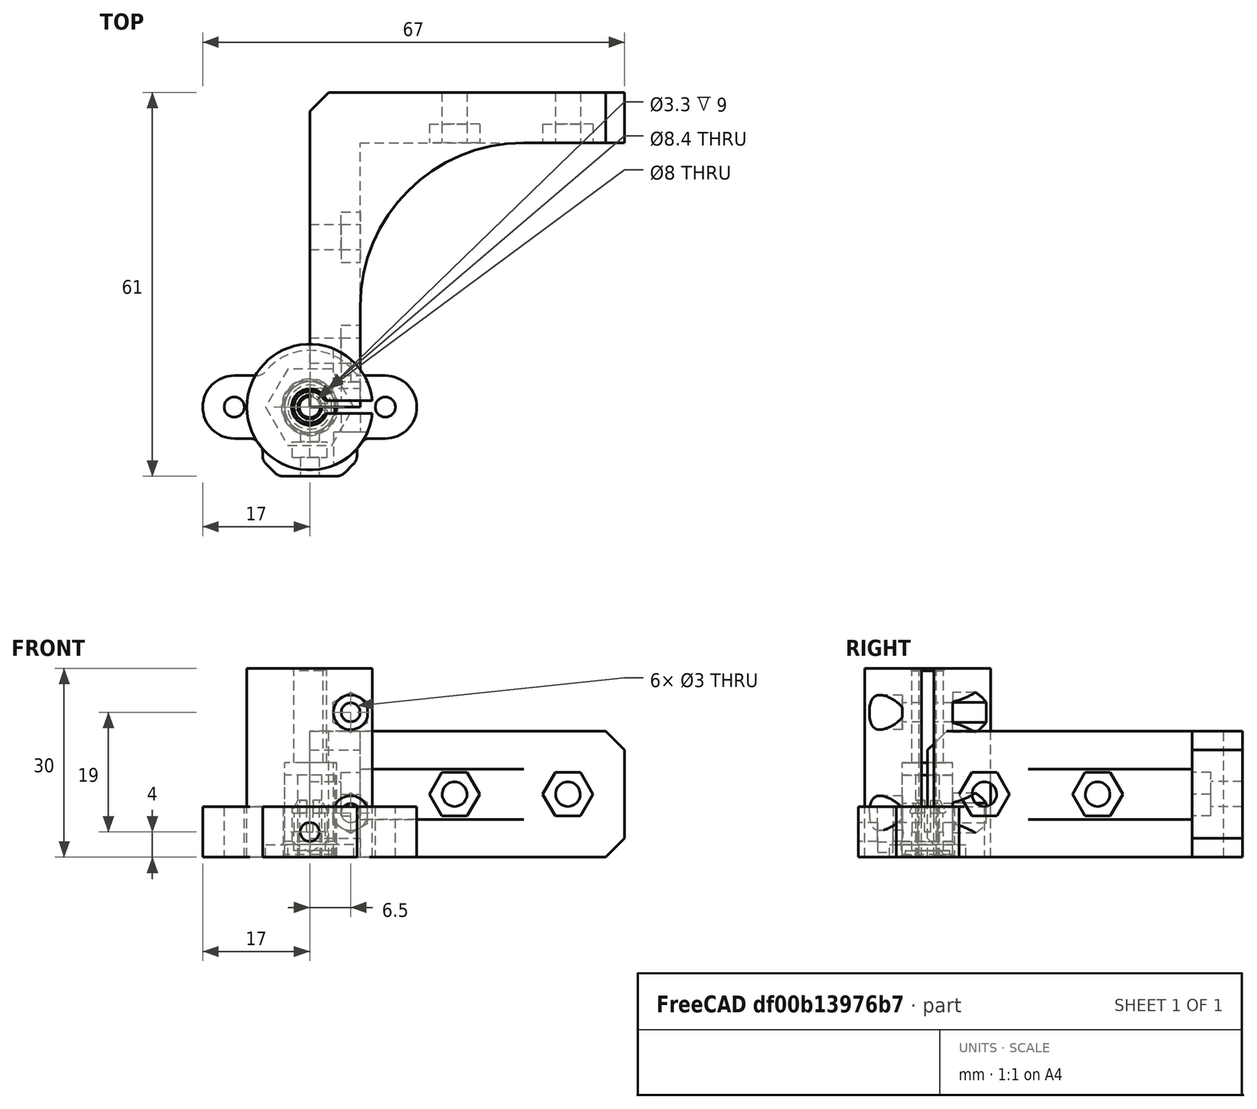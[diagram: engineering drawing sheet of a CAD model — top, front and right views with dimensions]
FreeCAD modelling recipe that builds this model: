
FCSTD DOCUMENT  (FreeCAD 0.16R6712 (Git))
Label: parts
License: All rights reserved
LicenseURL: http://en.wikipedia.org/wiki/All_rights_reserved
objects: Part::Cylinder×14, Part::MultiFuse×13, Part::Cut×9, Part::Chamfer×4, Part::Box×4, Sketcher::SketchObject×3, PartDesign::Pad×3, Part::Prism×3, Part::Fillet×3, Mesh::Feature×1, Part::Cone×1
note: 60 computed .brp shape members not serialized (recipe doc carries the construction recipe); baked Part::Feature solids carry a one-line shape summary decoded from their .brp

FEATURE [Mesh::Feature] Scuad_01
FEATURE [Sketcher::SketchObject] Sketch
  sketch-geometry (6):
    g0: LineSegment StartX=0 StartY=0 StartZ=0 EndX=8 EndY=0 EndZ=0
    g1: LineSegment StartX=8 StartY=0 StartZ=0 EndX=8 EndY=42 EndZ=0
    g2: LineSegment StartX=8 StartY=42 StartZ=0 EndX=50 EndY=42 EndZ=0
    g3: LineSegment StartX=50 StartY=42 StartZ=0 EndX=50 EndY=50 EndZ=0
    g4: LineSegment StartX=50 StartY=50 StartZ=0 EndX=0 EndY=50 EndZ=0
    g5: LineSegment StartX=0 StartY=50 StartZ=0 EndX=0 EndY=0 EndZ=0
  constraints (17):
    c: Coincident(g-1,g0)
    c: Coincident(g0,g1)
    c: Vertical(g1)
    c: Coincident(g1,g2)
    c: Horizontal(g2)
    c: Coincident(g2,g3)
    c: Vertical(g3)
    c: Coincident(g3,g4)
    c: Horizontal(g4)
    c: Coincident(g4,g5)
    c: Coincident(g5,g0)
    c: Vertical(g5)
    c: Horizontal(g0)
    c: Equal(g0,g3)
    c: Distance(g4) = 50
    c: Equal(g4,g5)
    c: Distance(g0) = 8
FEATURE [PartDesign::Pad] Pad
  Length = 20
  Length2 = 100
  Sketch = -> Sketch
  Type = 0
FEATURE [Part::Chamfer] Chamfer
  Base = -> Pad
  Edges = 5 edges r=3: [Edge3,Edge4,Edge12,Edge13,Edge14]
FEATURE [Part::Cylinder] Cylinder
  Angle = 360
  Height = 20
  Placement = pos=(-3,9,10) rot=(0,1,0;1.5708rad)
  Radius = 2
FEATURE [Part::Prism] Prism001
  Circumradius = 4
  Height = 14
  Placement = pos=(5,9,10) rot=(0.250563,0.935113,0.250563;1.63783rad)
  Polygon = 6
FEATURE [Part::MultiFuse] Fusion
  Placement = pos=(0,18,0) rot=(0,0,1;0rad)
  Shapes = -> [Cylinder,Prism001]
FEATURE [Part::MultiFuse] Fusion001
  Shapes = -> [Cylinder,Prism001]
FEATURE [Part::MultiFuse] Fusion002
  Placement = pos=(14,50,0) rot=(0,0,-1;1.5708rad)
  Shapes = -> [Cylinder,Prism001]
FEATURE [Part::MultiFuse] Fusion003
  Placement = pos=(32,50,0) rot=(0,0,-1;1.5708rad)
  Shapes = -> [Cylinder,Prism001]
FEATURE [Part::Box] Box  label="Cube"
  Height = 8
  Length = 36
  Placement = pos=(8,4,6) rot=(0,0,1;0rad)
  Width = 38
FEATURE [Part::Fillet] Fillet
  Base = -> Chamfer
  Edges = 1 edges r=26: [Edge16]
FEATURE [Part::Cut] Cut
  Base = -> Fillet
  Tool = -> Box
FEATURE [Part::MultiFuse] Fusion004
  Shapes = -> [Fusion003,Fusion002,Fusion,Fusion001]
FEATURE [Part::Cut] Cut001
  Base = -> Cut
  Tool = -> Fusion004
FEATURE [Sketcher::SketchObject] Sketch001
  sketch-geometry (15):
    g0: Circle CenterX=-12 CenterY=0 CenterZ=0 NormalX=0 NormalY=0 NormalZ=1 Radius=1.6
    g1: Circle CenterX=0 CenterY=0 CenterZ=0 NormalX=0 NormalY=0 NormalZ=1 Radius=4.2
    g2: Circle CenterX=12 CenterY=0 CenterZ=0 NormalX=0 NormalY=0 NormalZ=1 Radius=1.6
    g3: ArcOfCircle CenterX=-12 CenterY=0 CenterZ=0 NormalX=0 NormalY=0 NormalZ=1 Radius=5 StartAngle=1.5708 EndAngle=4.71238
    g4: ArcOfCircle CenterX=12 CenterY=0 CenterZ=0 NormalX=0 NormalY=0 NormalZ=1 Radius=5 StartAngle=4.71239 EndAngle=7.85398
    g5: LineSegment StartX=12 StartY=-5 StartZ=0 EndX=7.5 EndY=-5 EndZ=0
    g6: LineSegment StartX=7.5 StartY=-5 StartZ=0 EndX=7.5 EndY=-11 EndZ=0
    g7: LineSegment StartX=7.5 StartY=-11 StartZ=0 EndX=-7.5 EndY=-11 EndZ=0
    g8: LineSegment StartX=-7.5 StartY=-11 StartZ=0 EndX=-7.5 EndY=-5 EndZ=0
    g9: LineSegment StartX=-7.5 StartY=-5 StartZ=0 EndX=-12 EndY=-5 EndZ=0
    g10: LineSegment StartX=-12 StartY=5 StartZ=0 EndX=-7.48331 EndY=5 EndZ=0
    g11: LineSegment StartX=7.48331 StartY=5 StartZ=0 EndX=12 EndY=5 EndZ=0
    g12: ArcOfCircle CenterX=0 CenterY=0 CenterZ=0 NormalX=0 NormalY=0 NormalZ=1 Radius=9 StartAngle=0.589031 EndAngle=2.55256
    g13: LineSegment [constr] StartX=-12 StartY=0 StartZ=0 EndX=0 EndY=0 EndZ=0
    g14: LineSegment [constr] StartX=0 StartY=0 StartZ=0 EndX=12 EndY=0 EndZ=0
  constraints (42):
    c: Coincident(g3,g0)
    c: Coincident(g4,g2)
    c: Horizontal(g5)
    c: Coincident(g5,g6)
    c: Vertical(g6)
    c: Coincident(g6,g7)
    c: Horizontal(g7)
    c: Coincident(g7,g8)
    c: Vertical(g8)
    c: Coincident(g8,g9)
    c: Coincident(g9,g3)
    c: Horizontal(g9)
    c: Coincident(g10,g3)
    c: Horizontal(g10)
    c: Coincident(g11,g4)
    c: Horizontal(g11)
    c: Coincident(g12,g1)
    c: Coincident(g12,g10)
    c: Coincident(g13,g0)
    c: Coincident(g13,g1)
    c: Horizontal(g13)
    c: Coincident(g14,g1)
    c: Coincident(g14,g2)
    c: Horizontal(g14)
    c: Equal(g14,g13)
    c: Distance(g0,g2) = 24
    c: Radius(g0) = 1.6
    c: Equal(g0,g2)
    c: Radius(g4) = 5
    c: Equal(g4,g3)
    c: Coincident(g5,g4)
    c: Radius(g12) = 9
    c: Distance(g6) = 6
    c: Distance(g7) = 15
    c: Equal(g9,g5)
    c: Coincident(g12,g11)
    c: Equal(g10,g11)
    c: Tangent(g3,g9)
    c: Tangent(g5,g4)
    c: Radius(g1) = 4.2
    c: Tangent(g10,g3)
    c: Coincident(g-1,g1)
FEATURE [PartDesign::Pad] Pad001
  Length = 8
  Length2 = 100
  Sketch = -> Sketch001
  Type = 0
FEATURE [Part::Cylinder] Cylinder001
  Angle = 360
  Height = 15
  Placement = pos=(0,0,4) rot=(1,0,0;1.5708rad)
  Radius = 1.5
FEATURE [Sketcher::SketchObject] Sketch002
  Placement = pos=(0,-8,0) rot=(1,0,0;1.5708rad)
  sketch-geometry (10):
    g0: LineSegment StartX=0 StartY=0.8 StartZ=0 EndX=2.77128 EndY=2.4 EndZ=0
    g1: LineSegment StartX=2.77128 StartY=2.4 StartZ=0 EndX=2.77128 EndY=5.6 EndZ=0
    g2: LineSegment [constr] StartX=2.77128 StartY=5.6 StartZ=0 EndX=0 EndY=7.2 EndZ=0
    g3: LineSegment [constr] StartX=0 StartY=7.2 StartZ=0 EndX=-2.77128 EndY=5.6 EndZ=0
    g4: LineSegment StartX=-2.77128 StartY=5.6 StartZ=0 EndX=-2.77128 EndY=2.4 EndZ=0
    g5: LineSegment StartX=-2.77128 StartY=2.4 StartZ=0 EndX=0 EndY=0.8 EndZ=0
    g6: Circle [constr] CenterX=0 CenterY=4 CenterZ=0 NormalX=0 NormalY=0 NormalZ=1 Radius=3.2
    g7: LineSegment StartX=-2.77128 StartY=5.6 StartZ=0 EndX=-2.77128 EndY=11.6 EndZ=0
    g8: LineSegment StartX=-2.77128 StartY=11.6 StartZ=0 EndX=2.77128 EndY=11.6 EndZ=0
    g9: LineSegment StartX=2.77128 StartY=11.6 StartZ=0 EndX=2.77128 EndY=5.6 EndZ=0
  constraints (25):
    c: Coincident(g0,g1)
    c: Coincident(g1,g2)
    c: Coincident(g2,g3)
    c: Coincident(g3,g4)
    c: Coincident(g4,g5)
    c: Coincident(g5,g0)
    c: Equal(g0, g1-g5) x5
    c: PointOnObject(g0,g6)
    c: PointOnObject(g1,g6)
    c: PointOnObject(g2,g6)
    c: PointOnObject(g3,g6)
    c: PointOnObject(g4,g6)
    c: PointOnObject(g5,g6)
    c: PointOnObject(g6,g-2)
    c: PointOnObject(g0,g-2)
    c: Radius(g6) = 3.2
    c: Distance(g-1,g6) = 4
    c: Coincident(g3,g7)
    c: Vertical(g7)
    c: Coincident(g7,g8)
    c: Horizontal(g8)
    c: Coincident(g8,g9)
    c: Coincident(g9,g1)
    c: Vertical(g9)
    c: Distance(g7) = 6
FEATURE [PartDesign::Pad] Pad002
  Length = 2.5
  Length2 = 100
  Placement = pos=(0,-8,0) rot=(1,0,0;1.5708rad)
  Reversed = true
  Sketch = -> Sketch002
  Type = 0
FEATURE [Part::Chamfer] Chamfer001
  Base = -> Pad001
  Edges = 2 edges r=2.5: [Edge8,Edge11]
FEATURE [Part::Fillet] Fillet001
  Base = -> Chamfer001
  Edges = 8 edges r=2: [Edge2,Edge3,Edge19,Edge35,Edge37,Edge38,Edge39,Edge40]
FEATURE [Part::MultiFuse] Fusion005
  Shapes = -> [Pad002,Cylinder001]
FEATURE [Part::Cut] Cut002
  Base = -> Fillet001
  Tool = -> Fusion005
FEATURE [Part::Prism] Prism
  Circumradius = 7
  Height = 2
  Polygon = 6
FEATURE [Part::Cylinder] Cylinder002
  Angle = 360
  Height = 1.5
  Placement = pos=(0,0,1) rot=(0,0,1;0rad)
  Radius = 5
FEATURE [Part::Cylinder] Cylinder003
  Angle = 360
  Height = 10
  Placement = pos=(0,0,-1) rot=(0,0,1;0rad)
  Radius = 4
FEATURE [Part::Chamfer] Chamfer002
  Base = -> Cylinder002
  Edges = 1 edges r=1: [Edge1]
FEATURE [Part::MultiFuse] Fusion006
  Shapes = -> [Chamfer002,Prism]
FEATURE [Part::Cut] Cut003
  Base = -> Fusion006
  Tool = -> Cylinder003
FEATURE [Part::Cylinder] Cylinder004
  Angle = 360
  Height = 20
  Placement = pos=(0,0,-1) rot=(0,0,1;0rad)
  Radius = 1.9
FEATURE [Part::Cylinder] Cylinder005
  Angle = 360
  Height = 13
  Radius = 4
FEATURE [Part::Cut] Cut004
  Base = -> Cylinder005
  Tool = -> Cylinder004
FEATURE [Part::Cylinder] Cylinder006
  Angle = 360
  Height = 30
  Radius = 10
FEATURE [Part::Cylinder] Cylinder007
  Angle = 360
  Height = 16
  Placement = pos=(0,0,-1) rot=(0,0,1;0rad)
  Radius = 4
FEATURE [Part::Cylinder] Cylinder008
  Angle = 360
  Height = 32
  Placement = pos=(0,0,-1) rot=(0,0,1;0rad)
  Radius = 2.5
FEATURE [Part::Box] Box001  label="Cube001"
  Height = 32
  Length = 13
  Placement = pos=(0,-1,-1) rot=(0,0,1;0rad)
  Width = 2
FEATURE [Part::MultiFuse] Fusion007
  Shapes = -> [Cylinder007,Box001,Cylinder008]
FEATURE [Part::Cut] Cut005
  Base = -> Cylinder006
  Tool = -> Fusion007
FEATURE [Part::Cylinder] Cylinder009
  Angle = 360
  Height = 20
  Placement = pos=(0,0,-7) rot=(0,0,1;0rad)
  Radius = 1.5
FEATURE [Part::Prism] Prism002
  Circumradius = 3.2
  Height = 20
  Placement = pos=(0,0,-24) rot=(0,0,1;0.523599rad)
  Polygon = 6
FEATURE [Part::Cylinder] Cylinder010
  Angle = 360
  Height = 20
  Placement = pos=(0,0,4) rot=(0,0,1;0rad)
  Radius = 2.75
FEATURE [Part::MultiFuse] Fusion008
  Placement = pos=(6.5,0,7) rot=(1,0,0;1.5708rad)
  Shapes = -> [Cylinder009,Cylinder010,Prism002]
FEATURE [Part::MultiFuse] Fusion009
  Placement = pos=(6.5,0,23) rot=(1,0,0;1.5708rad)
  Shapes = -> [Cylinder009,Cylinder010,Prism002]
FEATURE [Part::MultiFuse] Fusion010
  Shapes = -> [Fusion008,Fusion009]
FEATURE [Part::Cut] Cut006
  Base = -> Cut005
  Tool = -> Fusion010
FEATURE [Part::Chamfer] Chamfer003
  Base = -> Cut006
  Edges = 6 edges r=0.4: [Edge24,Edge27,Edge29,Edge33,Edge35,Edge38]
FEATURE [Part::Cylinder] Cylinder011
  Angle = 360
  Height = 7.5
  Radius = 2.5
FEATURE [Part::Cylinder] Cylinder012
  Angle = 360
  Height = 1
  Radius = 3.5
FEATURE [Part::Box] Box002  label="Cube002"
  Height = 10
  Length = 1
  Placement = pos=(-0.5,-5,0) rot=(0,0,1;0rad)
  Width = 10
FEATURE [Part::Box] Box003  label="Cube003"
  Height = 10
  Length = 1
  Placement = pos=(5,-0.5,0) rot=(0,0,1;1.5708rad)
  Width = 10
FEATURE [Part::MultiFuse] Fusion011
  Placement = pos=(0,0,4) rot=(0,0,1;0rad)
  Shapes = -> [Box003,Box002]
FEATURE [Part::Cone] Cone
  Angle = 360
  Height = 2
  Placement = pos=(0,0,7) rot=(0,0,1;0rad)
  Radius1 = 3
  Radius2 = 2
FEATURE [Part::Fillet] Fillet002
  Base = -> Cone
  Edges = 1 edges r=0.2: [Edge3]
FEATURE [Part::Cylinder] Cylinder013
  Angle = 360
  Height = 14
  Placement = pos=(0,0,-1) rot=(0,0,1;0rad)
  Radius = 1.65
FEATURE [Part::MultiFuse] Fusion012
  Shapes = -> [Fillet002,Cylinder011,Cylinder012]
FEATURE [Part::Cut] Cut007
  Base = -> Fusion012
  Tool = -> Cylinder013
FEATURE [Part::Cut] Cut008
  Base = -> Cut007
  Tool = -> Fusion011
